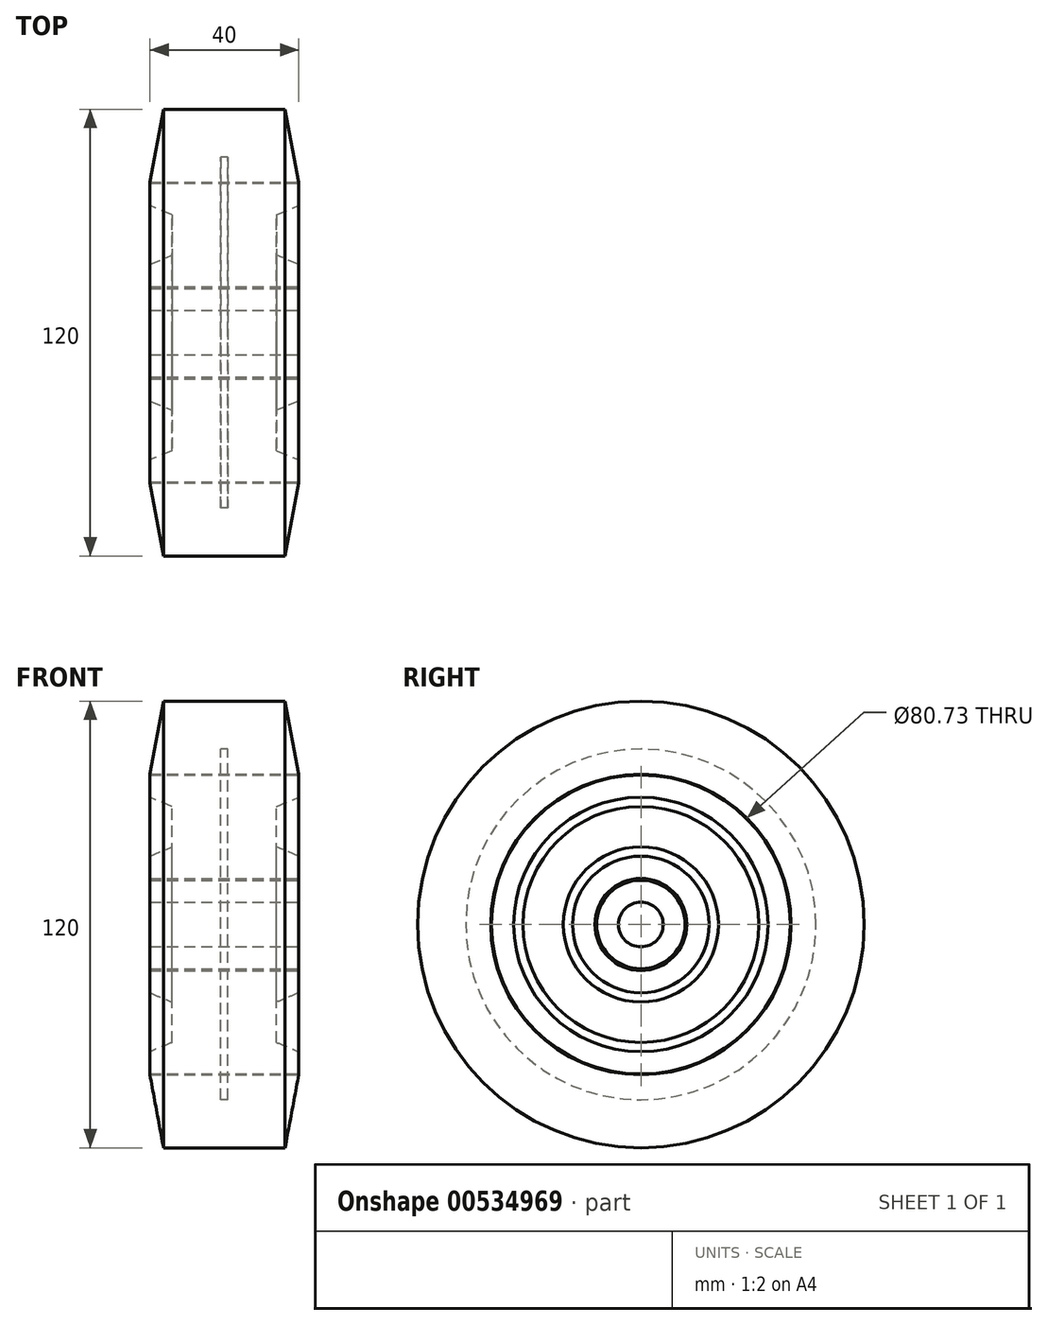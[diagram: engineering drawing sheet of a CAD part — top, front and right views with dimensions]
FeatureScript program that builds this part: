
annotation { "Feature Type Name" : "Feature", "Feature Type Description" : "" }
export const myFeature = defineFeature(function(context is Context, id is Id, definition is map)
    precondition{}
    {
        {
            var Q0;
            Q0=qCreatedBy(makeId("Front.planeOp"),FACE);
            var sketch = newSketch(context, id + "F0", { "sketchPlane" : qUnion([Q0])});
            skLineSegment(sketch, "E0", {"start": v(0, 0) * mm, "end": v(-133.33, 0) * mm, "construction": true});
            skLineSegment(sketch, "E1", {"start": v(0, -60) * mm, "end": v(-16.34, -60) * mm});
            skLineSegment(sketch, "E2", {"start": v(-16.34, -60) * mm, "end": v(-20, -40.37) * mm});
            skLineSegment(sketch, "E3", {"start": v(-20, -40.37) * mm, "end": v(0, -40.37) * mm});
            skLineSegment(sketch, "E4", {"start": v(0, -40.37) * mm, "end": v(0, -60) * mm, "construction": true});
            skLineSegment(sketch, "E5", {"start": v(0, -40.37) * mm, "end": v(-20, -40.37) * mm});
            skLineSegment(sketch, "E6", {"start": v(-20, -40.17) * mm, "end": v(-20, -34.17) * mm});
            skLineSegment(sketch, "E7", {"start": v(-20, -34.17) * mm, "end": v(-14.08, -31.69) * mm});
            skLineSegment(sketch, "E8", {"start": v(-14.08, -31.69) * mm, "end": v(-14.08, -20.84) * mm});
            skLineSegment(sketch, "E9", {"start": v(-14.08, -20.84) * mm, "end": v(-20, -18.36) * mm});
            skLineSegment(sketch, "E10", {"start": v(-20, -18.36) * mm, "end": v(-20, -12.36) * mm});
            skLineSegment(sketch, "E11", {"start": v(-20, -12.36) * mm, "end": v(0, -12.36) * mm});
            skLineSegment(sketch, "E12", {"start": v(0, -12.36) * mm, "end": v(0, -40.37) * mm, "construction": true});
            skLineSegment(sketch, "E13", {"start": v(0, -11.9) * mm, "end": v(-20, -11.9) * mm});
            skLineSegment(sketch, "E14", {"start": v(-20, -11.9) * mm, "end": v(-20, -6) * mm});
            skLineSegment(sketch, "E15", {"start": v(-20, -6) * mm, "end": v(0, -6) * mm});
            skLineSegment(sketch, "E16", {"start": v(0, -6) * mm, "end": v(0, -11.9) * mm, "construction": true});
            skLineSegment(sketch, "E17.MirrorCS", {"start": v(14.08, -20.84) * mm, "end": v(20, -18.36) * mm});
            skLineSegment(sketch, "E18.MirrorCS", {"start": v(20, -18.36) * mm, "end": v(20, -12.36) * mm});
            skLineSegment(sketch, "E19.MirrorCS", {"start": v(20, -12.36) * mm, "end": v(0, -12.36) * mm});
            skLineSegment(sketch, "E20.MirrorCS", {"start": v(0, -11.9) * mm, "end": v(20, -11.9) * mm});
            skLineSegment(sketch, "E21.MirrorCS", {"start": v(20, -11.9) * mm, "end": v(20, -6) * mm});
            skLineSegment(sketch, "E22.MirrorCS", {"start": v(20, -6) * mm, "end": v(0, -6) * mm});
            skLineSegment(sketch, "E23.MirrorCS", {"start": v(0, -40.37) * mm, "end": v(20, -40.37) * mm});
            skLineSegment(sketch, "E24.MirrorCS", {"start": v(20, -40.37) * mm, "end": v(20, -34.17) * mm});
            skLineSegment(sketch, "E25.MirrorCS", {"start": v(20, -34.17) * mm, "end": v(14.08, -31.69) * mm});
            skLineSegment(sketch, "E26.MirrorCS", {"start": v(14.08, -31.69) * mm, "end": v(14.08, -20.84) * mm});
            skLineSegment(sketch, "E27.MirrorCS", {"start": v(16.34, -60) * mm, "end": v(20, -40.37) * mm});
            skLineSegment(sketch, "E28.MirrorCS", {"start": v(20, -40.37) * mm, "end": v(0, -40.37) * mm});
            skLineSegment(sketch, "E29.MirrorCS", {"start": v(0, -60) * mm, "end": v(16.34, -60) * mm});
            skLineSegment(sketch, "E30", {"start": v(-20, -40.17) * mm, "end": v(0, -40.17) * mm});
            skLineSegment(sketch, "E31.MirrorCS", {"start": v(20, -40.17) * mm, "end": v(0, -40.17) * mm});
            skSolve(sketch);
        }
        {
            var Q0;
            Q0=makeQuery(id+"F0.imprint","IMPRINT",FACE,{"disambiguationData":[TD([[makeQuery(id+"F0.imprint","IMPRINT",EDGE,{"derivedFrom":sQuery(id+"F0.wireOp",EDGE,"E13")}),-1.0]])]});
            var Q1;
            Q1=makeQuery(id+"F0.imprint","IMPRINT",FACE,{"disambiguationData":[TD([[makeQuery(id+"F0.imprint","IMPRINT",EDGE,{"derivedFrom":sQuery(id+"F0.wireOp",EDGE,"E5")}),-1.0]])]});
            var Q2;
            Q2=makeQuery(id+"F0.imprint","IMPRINT",FACE,{"disambiguationData":[TD([[makeQuery(id+"F0.imprint","IMPRINT",EDGE,{"derivedFrom":sQuery(id+"F0.wireOp",EDGE,"E1")}),-1.0]])]});
            var Q3;
            Q3=makeQuery(id+"F0.imprint","IMPRINT",FACE,{"disambiguationData":[TD([[makeQuery(id+"F0.imprint","IMPRINT",EDGE,{"derivedFrom":sQuery(id+"F0.wireOp",EDGE,"E6")}),-1.0]])]});
            var Q4;
            Q4=sQuery(id+"F0.wireOp",EDGE,"E0");
            revolve(context, id + "F1", {"entities" : qUnion([Q0, Q1, Q2, Q3]), "axis" : qUnion([Q4]), "revolveType" : RevolveType.FULL});
        }
        {
            var Q0;
            Q0=qCreatedBy(makeId("Right.planeOp"),FACE);
            var sketch = newSketch(context, id + "F2", { "sketchPlane" : qUnion([Q0])});
            skCircle(sketch, "E32", {"center": v(0, 0) * mm, "radius": 47.1 * mm});
            skSolve(sketch);
        }
        {
            var Q0;
            Q0 = qSketchRegion(id + "F2", true);
            extrude(context, id + "F3", {"entities" : qUnion([Q0]), "depth" : 2 * mm, "offsetDistance" : 25 * mm, "symmetric" : true});
        }
    });
